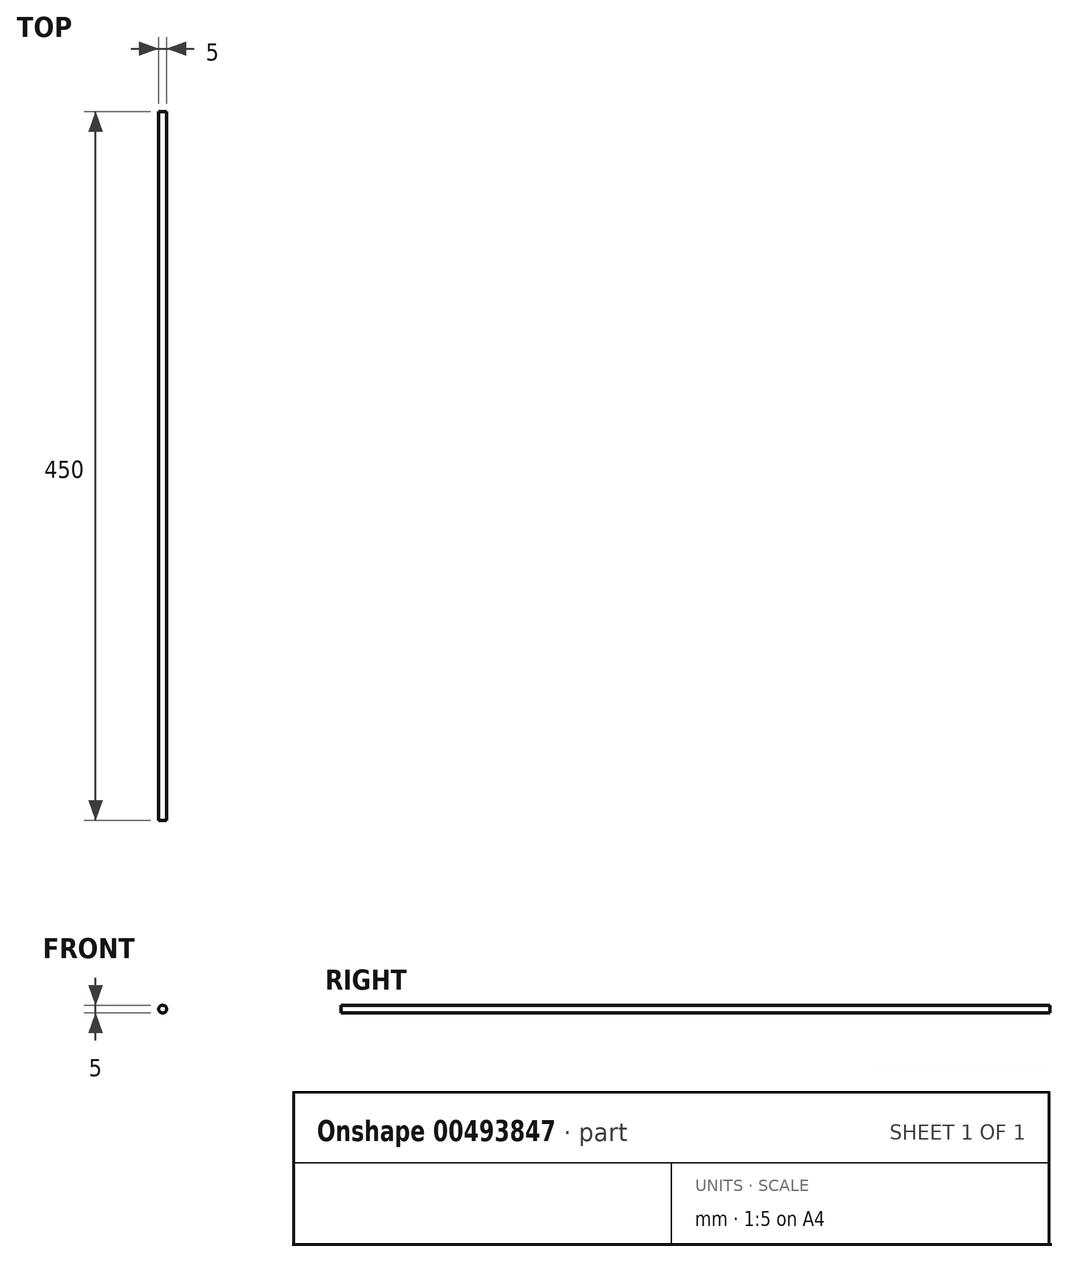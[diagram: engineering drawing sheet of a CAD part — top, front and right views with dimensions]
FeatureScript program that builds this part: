
annotation { "Feature Type Name" : "Feature", "Feature Type Description" : "" }
export const myFeature = defineFeature(function(context is Context, id is Id, definition is map)
    precondition{}
    {
        {
            var Q0;
            Q0=qCreatedBy(makeId("Front.planeOp"),FACE);
            var sketch = newSketch(context, id + "F0", { "sketchPlane" : qUnion([Q0])});
            skCircle(sketch, "E0", {"center": v(-124.3, 5.98) * mm, "radius": 2.5 * mm});
            skSolve(sketch);
        }
        {
            var Q0;
            Q0 = qSketchRegion(id + "F0", true);
            extrude(context, id + "F1", {"entities" : qUnion([Q0]), "depth" : 450 * mm});
        }
    });
